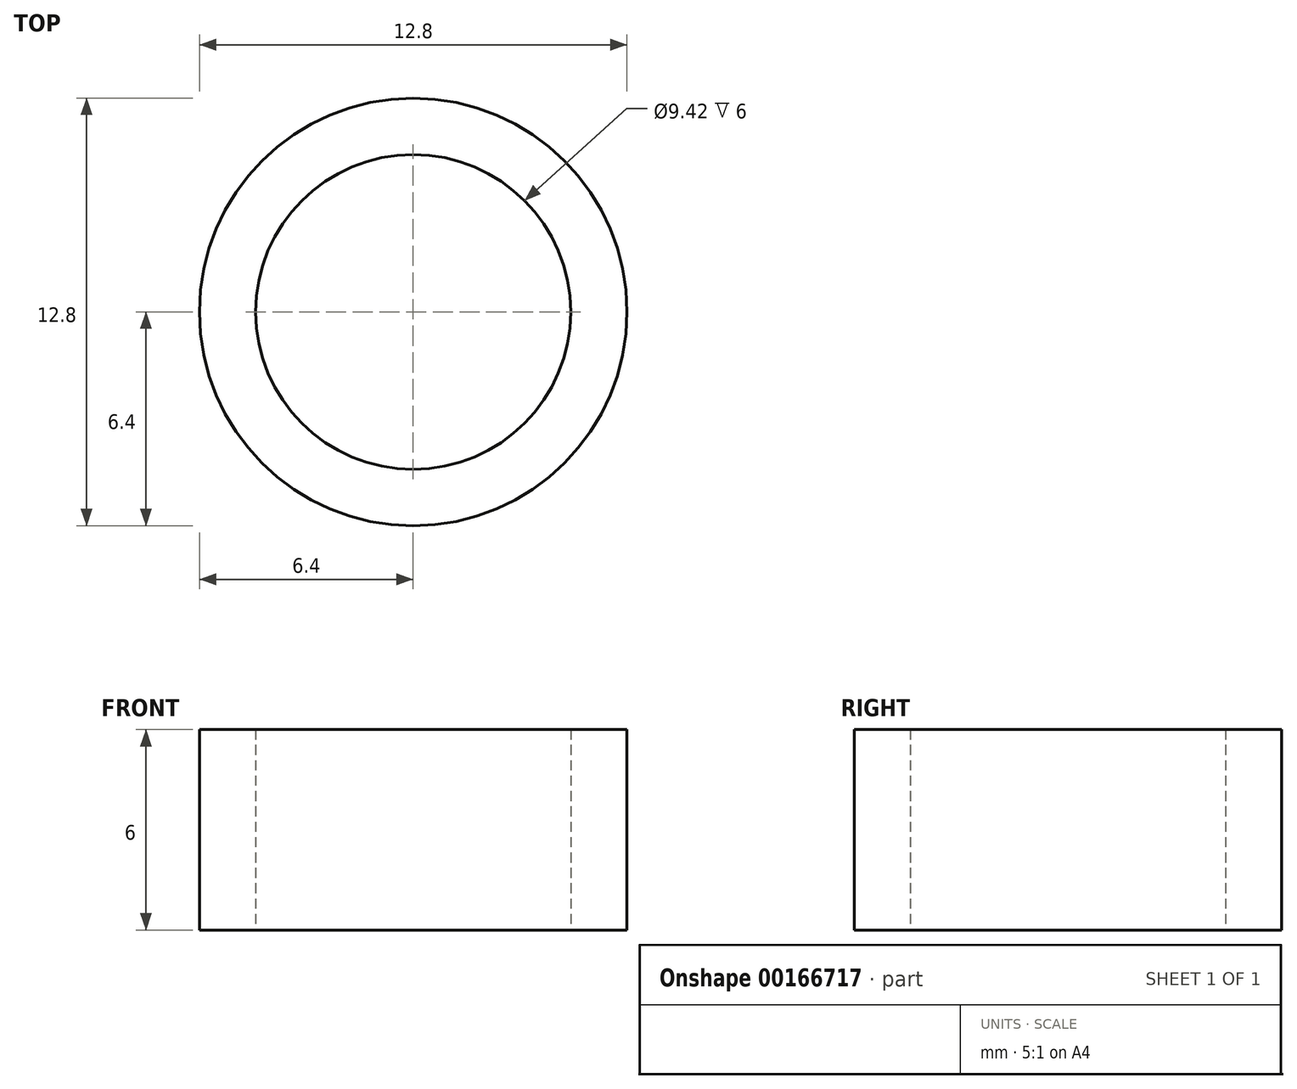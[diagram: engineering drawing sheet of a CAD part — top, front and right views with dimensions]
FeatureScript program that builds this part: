
annotation { "Feature Type Name" : "Feature", "Feature Type Description" : "" }
export const myFeature = defineFeature(function(context is Context, id is Id, definition is map)
    precondition{}
    {
        {
            var Q0;
            Q0=qCreatedBy(makeId("Top.planeOp"),FACE);
            var sketch = newSketch(context, id + "F0", { "sketchPlane" : qUnion([Q0])});
            skCircle(sketch, "E0", {"center": v(0, 0) * mm, "radius": 4.71 * mm});
            skCircle(sketch, "E1", {"center": v(0, 0) * mm, "radius": 6.4 * mm});
            skSolve(sketch);
        }
        {
            var Q0;
            Q0 = qSketchRegion(id + "F0", true);
            extrude(context, id + "F1", {"entities" : qUnion([Q0]), "depth" : 6 * mm});
        }
    });
